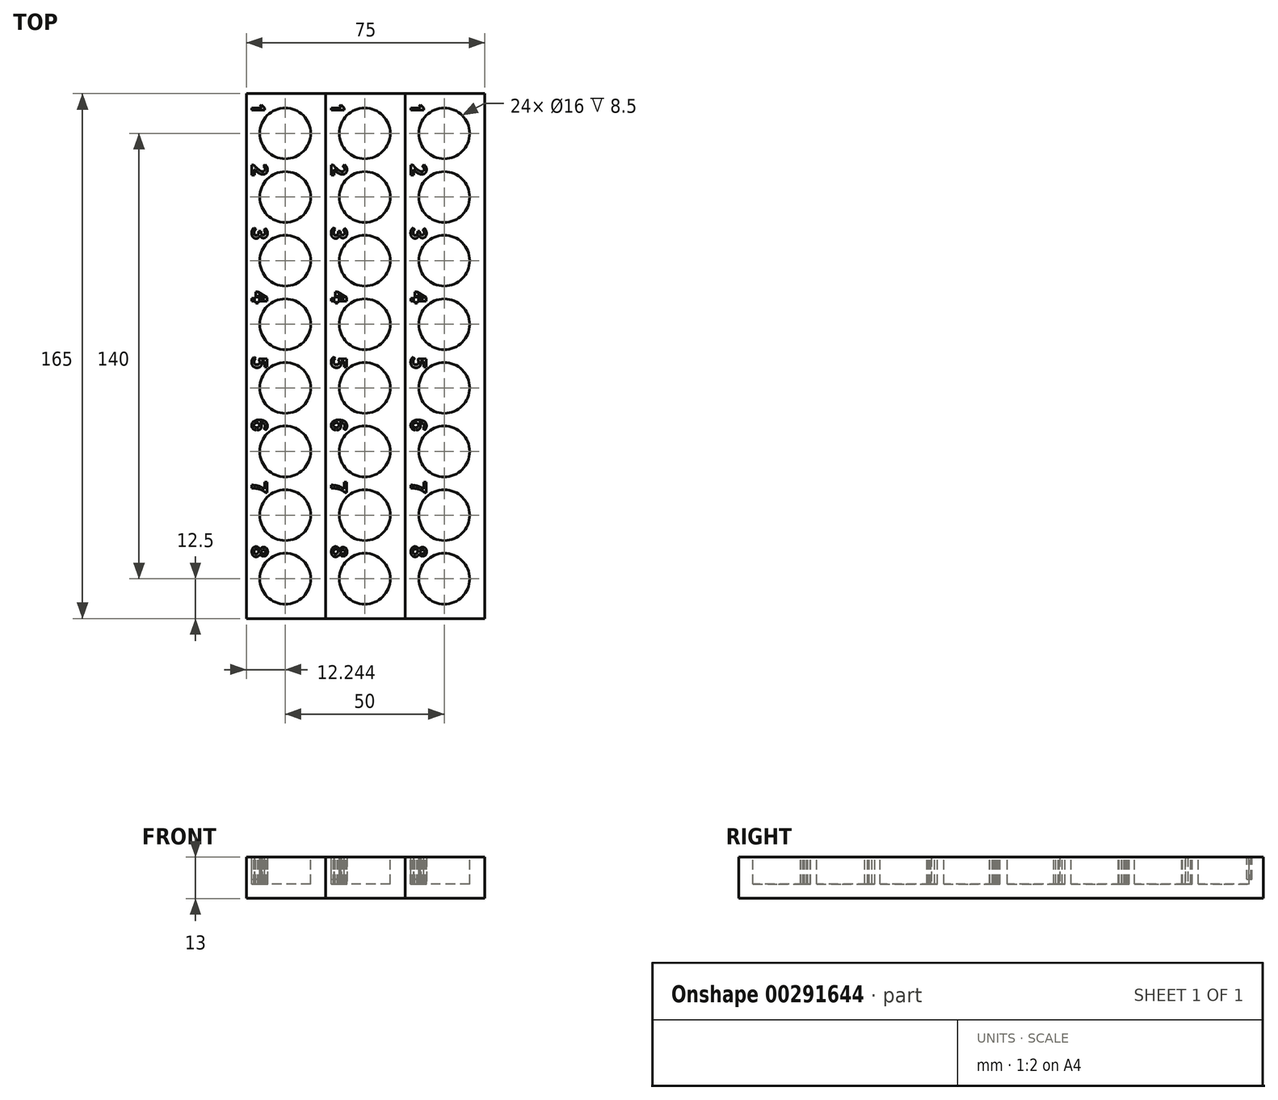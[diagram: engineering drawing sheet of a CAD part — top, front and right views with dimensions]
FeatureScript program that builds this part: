
annotation { "Feature Type Name" : "Feature", "Feature Type Description" : "" }
export const myFeature = defineFeature(function(context is Context, id is Id, definition is map)
    precondition{}
    {
        {
            var Q0;
            Q0=qCreatedBy(makeId("Front.planeOp"),FACE);
            var sketch = newSketch(context, id + "F0", { "sketchPlane" : qUnion([Q0])});
            skLineSegment(sketch, "E0.bottom", {"start": v(-8.6, -0.88) * mm, "end": v(16.4, -0.88) * mm});
            skLineSegment(sketch, "E0.top", {"start": v(-8.6, -13.88) * mm, "end": v(16.4, -13.88) * mm});
            skLineSegment(sketch, "E0.left", {"start": v(-8.6, -0.88) * mm, "end": v(-8.6, -13.88) * mm});
            skLineSegment(sketch, "E0.right", {"start": v(16.4, -0.88) * mm, "end": v(16.4, -13.88) * mm});
            skSolve(sketch);
        }
        {
            var Q0;
            Q0 = qSketchRegion(id + "F0", true);
            extrude(context, id + "F1", {"entities" : qUnion([Q0]), "depth" : 165 * mm});
        }
        {
            var Q0;
            Q0=makeQuery(id+"F1.opExtrude","SWEPT_FACE",FACE,{"disambiguationData":[OSD([sQuery(id+"F0.wireOp",EDGE,"E0.bottom")])]});
            var sketch = newSketch(context, id + "F2", { "sketchPlane" : qUnion([Q0])});
            skCircle(sketch, "E1", {"center": v(3.64, -152.5) * mm, "radius": 8 * mm});
            skCircle(sketch, "E2", {"center": v(3.64, -132.5) * mm, "radius": 8 * mm});
            skCircle(sketch, "E3", {"center": v(3.64, -112.5) * mm, "radius": 8 * mm});
            skCircle(sketch, "E4", {"center": v(3.64, -92.5) * mm, "radius": 8 * mm});
            skCircle(sketch, "E5", {"center": v(3.64, -72.5) * mm, "radius": 8 * mm});
            skCircle(sketch, "E6", {"center": v(3.64, -52.5) * mm, "radius": 8 * mm});
            skCircle(sketch, "E7", {"center": v(3.64, -32.5) * mm, "radius": 8 * mm});
            skCircle(sketch, "E8", {"center": v(3.64, -12.5) * mm, "radius": 8 * mm});
            skText(sketch, "E9", { "text": "1", "fontName": "AllertaStencil-Regular.ttf"});
            skText(sketch, "E10", { "text": "2", "fontName": "NotoSansCJKtc-Bold.otf"});
            skText(sketch, "E11", { "text": "3", "fontName": "NotoSansCJKtc-Bold.otf"});
            skText(sketch, "E12", { "text": "4", "fontName": "NotoSansCJKtc-Bold.otf"});
            skText(sketch, "E13", { "text": "5", "fontName": "NotoSansCJKtc-Bold.otf"});
            skText(sketch, "E14", { "text": "6", "fontName": "NotoSansCJKtc-Bold.otf"});
            skText(sketch, "E15", { "text": "7", "fontName": "NotoSansCJKtc-Bold.otf"});
            skText(sketch, "E16", { "text": "8", "fontName": "NotoSansCJKtc-Bold.otf"});
            const initialGuessF2  = {"E9": [-0.00685, -0.00337, 0, -1, 0.004], "E10": [-0.00685, -0.02211, 0, -1, 0.0047], "E11": [-0.00685, -0.04206, 0, -1, 0.0047], "E12": [-0.00685, -0.0622, 0, -1, 0.0047], "E13": [-0.00685, -0.08268, 0, -1, 0.0047], "E14": [-0.00685, -0.10223, 0, -1, 0.0047], "E15": [-0.00685, -0.12183, 0, -1, 0.0047], "E16": [-0.00679, -0.14207, 0, -1, 0.0047]};
            skSetInitialGuess(sketch, initialGuessF2);
            skSolve(sketch);
        }
        {
            var Q0;
            Q0 = qSketchRegion(id + "F2", true);
            extrude(context, id + "F3", {"entities" : qUnion([Q0]), "operationType" : NewBodyOperationType.REMOVE, "oppositeDirection" : true, "depth" : 8.5 * mm});
        }
        {
            var Q0;
            Q0=makeQuery(id+"F3.boolean.opBoolean","COPY",FACE,{"derivedFrom":makeQuery(id+"F3.opExtrude","CAP_FACE",FACE,{"disambiguationData":[OSD([sQuery(id+"F2.wireOp",EDGE,"E9.sketch_text.stroke-0"),sQuery(id+"F2.wireOp",EDGE,"E9.sketch_text.stroke-1"),sQuery(id+"F2.wireOp",EDGE,"E9.sketch_text.stroke-2"),sQuery(id+"F2.wireOp",EDGE,"E9.sketch_text.stroke-3"),sQuery(id+"F2.wireOp",EDGE,"E9.sketch_text.stroke-4"),sQuery(id+"F2.wireOp",EDGE,"E9.sketch_text.stroke-5"),sQuery(id+"F2.wireOp",EDGE,"E9.sketch_text.stroke-6")])],"isStart":false})});
            extrude(context, id + "F4", {"entities" : qUnion([Q0]), "operationType" : NewBodyOperationType.ADD, "depth" : 1.5 * mm});
        }
        {
            var Q0;
            Q0=makeQuery(id+"F1.opExtrude","SWEPT_BODY",BODY,{"disambiguationData":[OSD([sQuery(id+"F0.wireOp",EDGE,"E0.bottom"),sQuery(id+"F0.wireOp",EDGE,"E0.top"),sQuery(id+"F0.wireOp",EDGE,"E0.left"),sQuery(id+"F0.wireOp",EDGE,"E0.right")])]});
            transform(context, id + "F5", {"entities" : qUnion([Q0]), "transformType" : TransformType.TRANSLATION_3D, "dx" : 0 * mm, "dy" : 0 * mm, "dz" : 0 * mm, "makeCopy" : true});
        }
        {
            var Q0;
            Q0=makeQuery(id+"F5.opPattern","COPY",BODY,{"derivedFrom":makeQuery(id+"F1.opExtrude","SWEPT_BODY",BODY,{"disambiguationData":[OSD([sQuery(id+"F0.wireOp",EDGE,"E0.bottom"),sQuery(id+"F0.wireOp",EDGE,"E0.top"),sQuery(id+"F0.wireOp",EDGE,"E0.left"),sQuery(id+"F0.wireOp",EDGE,"E0.right")])]}),"instanceName":"1"});
            deleteBodies(context, id + "F6", {"entities" : qUnion([Q0])});
        }
        {
            var Q0;
            Q0=makeQuery(id+"F1.opExtrude","SWEPT_BODY",BODY,{"disambiguationData":[OSD([sQuery(id+"F0.wireOp",EDGE,"E0.bottom"),sQuery(id+"F0.wireOp",EDGE,"E0.top"),sQuery(id+"F0.wireOp",EDGE,"E0.left"),sQuery(id+"F0.wireOp",EDGE,"E0.right")])]});
            var Q1;
            Q1=makeQuery(id+"F1.opExtrude","SWEPT_EDGE",EDGE,{"disambiguationData":[OSD([sQuery(id+"F0.wireOp",EDGE,"E0.top"),sQuery(id+"F0.wireOp",EDGE,"E0.right")])]});
            transform(context, id + "F7", {"entities" : qUnion([Q0]), "transformType" : TransformType.TRANSLATION_ENTITY, "oppositeDirectionEntity" : false, "transformLine" : qUnion([Q1]), "makeCopy" : true});
        }
        {
            var Q0;
            Q0=makeQuery(id+"F7.opPattern","COPY",BODY,{"derivedFrom":makeQuery(id+"F1.opExtrude","SWEPT_BODY",BODY,{"disambiguationData":[OSD([sQuery(id+"F0.wireOp",EDGE,"E0.bottom"),sQuery(id+"F0.wireOp",EDGE,"E0.top"),sQuery(id+"F0.wireOp",EDGE,"E0.left"),sQuery(id+"F0.wireOp",EDGE,"E0.right")])]}),"instanceName":"1"});
            deleteBodies(context, id + "F8", {"entities" : qUnion([Q0])});
        }
        {
            var Q0;
            Q0=makeQuery(id+"F1.opExtrude","SWEPT_BODY",BODY,{"disambiguationData":[OSD([sQuery(id+"F0.wireOp",EDGE,"E0.bottom"),sQuery(id+"F0.wireOp",EDGE,"E0.top"),sQuery(id+"F0.wireOp",EDGE,"E0.left"),sQuery(id+"F0.wireOp",EDGE,"E0.right")])]});
            var Q1;
            Q1=makeQuery(id+"F1.opExtrude","CAP_VERTEX",VERTEX,{"disambiguationData":[OSD([sQuery(id+"F0.wireOp",EDGE,"E0.bottom"),sQuery(id+"F0.wireOp",EDGE,"E0.left")])],"isStart":false});
            var Q2;
            Q2=makeQuery(id+"F1.opExtrude","CAP_VERTEX",VERTEX,{"disambiguationData":[OSD([sQuery(id+"F0.wireOp",EDGE,"E0.bottom"),sQuery(id+"F0.wireOp",EDGE,"E0.right")])],"isStart":false});
            transform(context, id + "F9", {"entities" : qUnion([Q0]), "transformType" : TransformType.TRANSLATION_ENTITY, "oppositeDirectionEntity" : false, "transformLine" : qUnion([Q1, Q2]), "makeCopy" : true});
        }
        {
            var Q0;
            Q0=makeQuery(id+"F9.opPattern","COPY",BODY,{"derivedFrom":makeQuery(id+"F1.opExtrude","SWEPT_BODY",BODY,{"disambiguationData":[OSD([sQuery(id+"F0.wireOp",EDGE,"E0.bottom"),sQuery(id+"F0.wireOp",EDGE,"E0.top"),sQuery(id+"F0.wireOp",EDGE,"E0.left"),sQuery(id+"F0.wireOp",EDGE,"E0.right")])]}),"instanceName":"1"});
            var Q1;
            Q1=makeQuery(id+"F1.opExtrude","CAP_VERTEX",VERTEX,{"disambiguationData":[OSD([sQuery(id+"F0.wireOp",EDGE,"E0.bottom"),sQuery(id+"F0.wireOp",EDGE,"E0.right")])],"isStart":false});
            var Q2;
            Q2=makeQuery(id+"F9.opPattern","COPY",VERTEX,{"derivedFrom":makeQuery(id+"F1.opExtrude","CAP_VERTEX",VERTEX,{"disambiguationData":[OSD([sQuery(id+"F0.wireOp",EDGE,"E0.bottom"),sQuery(id+"F0.wireOp",EDGE,"E0.right")])],"isStart":false}),"instanceName":"1"});
            transform(context, id + "F10", {"entities" : qUnion([Q0]), "transformType" : TransformType.TRANSLATION_ENTITY, "oppositeDirectionEntity" : false, "transformLine" : qUnion([Q1, Q2]), "makeCopy" : true});
        }
    });
